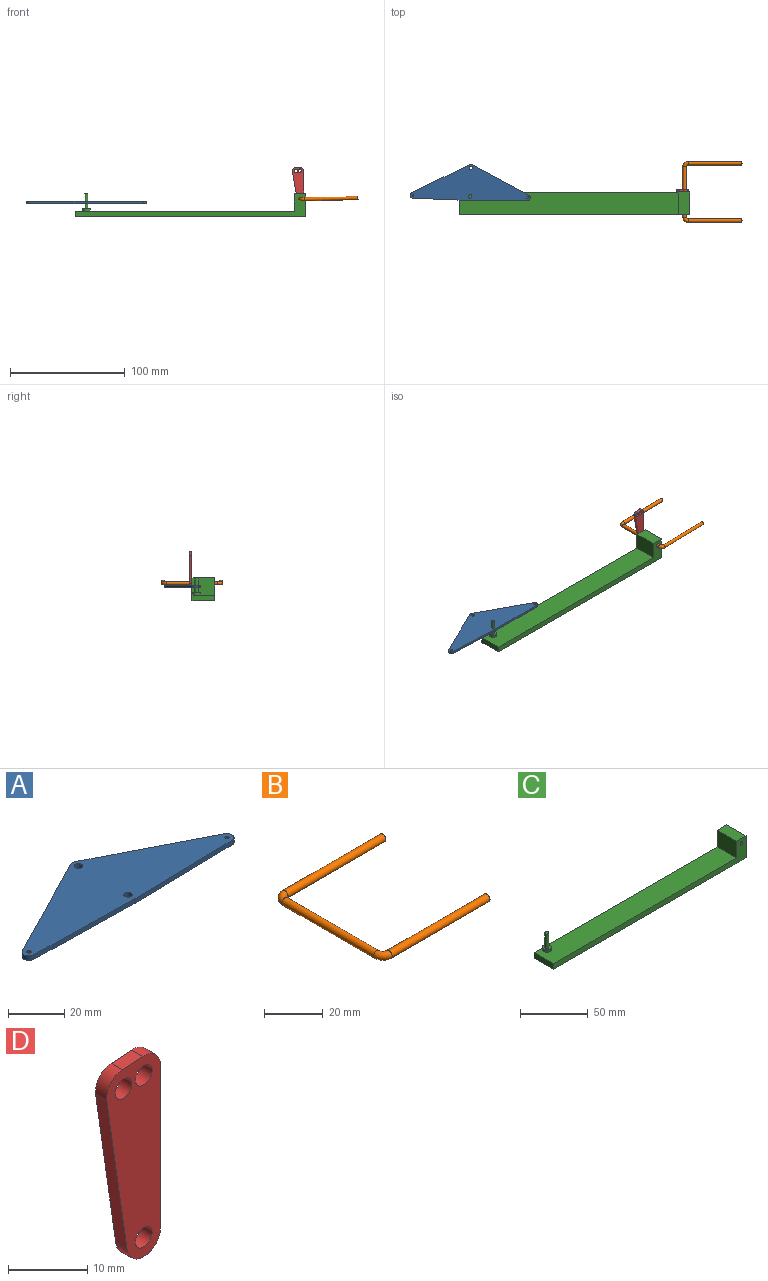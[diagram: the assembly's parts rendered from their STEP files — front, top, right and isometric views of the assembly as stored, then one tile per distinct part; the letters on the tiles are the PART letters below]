
ASSEMBLY  parts=4 mates=3
PART A: 14 faces, bbox 105x31.5x2 mm
  f0: plane 49.77x25.45mm, normal (-0.46,0.89,0), area 111.8mm2, adj f1,f11,f12,f13
  f1: cylinder r=2.5mm len=4.73mm, axis (0,0,1), area 13.2mm2, adj f0,f2,f12,f13
  f2: plane 49.98x2mm, normal (-0.02,-1,0), area 100mm2, adj f1,f3,f12,f13
  f3: plane 2x0.14mm, normal (0,-1,0), area 0.3mm2, adj f2,f4,f12,f13
  f4: plane 49.98x2mm, normal (0.02,-1,0), area 100mm2, adj f3,f5,f12,f13
  f5: cylinder r=2.5mm len=4.73mm, axis (0,0,1), area 13.2mm2, adj f4,f6,f12,f13
  f6: plane 49.77x25.45mm, normal (0.46,0.89,0), area 111.8mm2, adj f5,f11,f12,f13
  f7: cylinder r=0.75mm len=2mm, axis (0,0,1), area 9.4mm2, adj f12,f13
  f8: cylinder r=0.75mm len=2mm, axis (0,0,1), area 9.4mm2, adj f12,f13
  f9: cylinder r=1.5mm len=3mm, axis (0,0,1), area 18.8mm2, adj f12,f13
  f10: cylinder r=1.5mm len=3mm, axis (0,0,1), area 18.8mm2, adj f12,f13
  f11: cylinder r=3mm len=2.73mm, axis (0,0,1), area 5.7mm2, adj f0,f6,f12,f13
  f12: plane 105x31.5mm, normal (0,0,1), area 1860.8mm2, adj f0,f1,f2,f3,f4,f5,f6,f7
  f13: plane 105x31.5mm, normal (0,0,-1), area 1860.8mm2, adj f0,f1,f2,f3,f4,f5,f6,f7
PART B: 7 faces, bbox 51.9x53.7x3 mm
  f0: plane 3x3mm, normal (1,0,0), area 7.1mm2, adj f2
  f1: plane 3x3mm, normal (1,0,0), area 7.1mm2, adj f6
  f2: cylinder r=1.5mm len=47mm, axis (-1,0,0), area 443mm2, adj f0,f3
  f3: torus R=3mm, axis (0,0,1), area 44.4mm2, adj f2,f4
  f4: cylinder r=1.5mm len=44mm, axis (0,-1,0), area 414.7mm2, adj f3,f5
  f5: torus R=3mm, axis (0,0,1), area 44.4mm2, adj f4,f6
  f6: cylinder r=1.5mm len=47mm, axis (1,0,0), area 443mm2, adj f1,f5
PART C: 13 faces, bbox 201.1x20x20 mm
  f0: plane 201.05x20mm, normal (0,-1,0), area 1148.2mm2, adj f2,f3,f4,f9,f10,f11,f12
  f1: plane 201.05x20mm, normal (0,1,0), area 1148.2mm2, adj f2,f3,f4,f9,f10,f11,f12
  f2: plane 20x5mm, normal (-1,0,0), area 100mm2, adj f0,f1,f3,f4
  f3: plane 191.05x20mm, normal (0,0,1), area 3785.5mm2, adj f0,f1,f2,f5,f9
  f4: plane 201.05x20mm, normal (0,0,-1), area 4021.1mm2, adj f0,f1,f2,f10
  f5: cylinder r=3.36mm len=6.73mm, axis (0,0,1), area 42.3mm2, adj f3,f6
  f6: plane 6.73x6.73mm, normal (0,0,1), area 28.5mm2, adj f5,f7
  f7: cylinder r=1.5mm len=13mm, axis (0,0,1), area 122.5mm2, adj f6,f8
  f8: plane 3x3mm, normal (0,0,1), area 7.1mm2, adj f7
  f9: plane 20x15mm, normal (-1,0,0), area 300mm2, adj f0,f1,f3,f11
  f10: plane 20x20mm, normal (1,0,0), area 400mm2, adj f0,f1,f4,f11
  f11: plane 20x10mm, normal (0,0,1), area 200mm2, adj f0,f1,f9,f10
  f12: cylinder r=1.5mm len=20mm, axis (0,1,0), area 188.5mm2, adj f0,f1
PART D: 11 faces, bbox 9.6x2x31 mm
  f0: cylinder r=3mm len=5.97mm, axis (0,-1,0), area 18mm2, adj f1,f8,f9,f10
  f1: plane 25x2mm, normal (1,0,0), area 50mm2, adj f0,f2,f9,f10
  f2: cylinder r=3mm len=3.22mm, axis (0,-1,0), area 9.9mm2, adj f1,f3,f9,f10
  f3: plane 3.6x2mm, normal (-0.07,0,1), area 7.2mm2, adj f2,f4,f9,f10
  f4: cylinder r=3mm len=3.42mm, axis (0,-1,0), area 9.9mm2, adj f3,f8,f9,f10
  f5: cylinder r=1.5mm len=3mm, axis (0,-1,0), area 18.8mm2, adj f9,f10
  f6: cylinder r=1.5mm len=3mm, axis (0,-1,0), area 18.8mm2, adj f9,f10
  f7: cylinder r=1.5mm len=3mm, axis (0,-1,0), area 18.8mm2, adj f9,f10
  f8: plane 24.74x3.6mm, normal (-0.99,0,-0.14), area 50mm2, adj f0,f4,f9,f10
  f9: plane 31x9.6mm, normal (0,-1,0), area 212.9mm2, adj f0,f1,f2,f3,f4,f5,f6,f7
  f10: plane 31x9.6mm, normal (0,1,0), area 212.9mm2, adj f0,f1,f2,f3,f4,f5,f6,f7
PLACE A rot(axis=(0,0,-1),1.2deg) t=(39.99,-7.96,8.66)mm
PLACE B rot(axis=(0,-1,0),1.3deg) t=(236.19,-31.37,13.65)mm
PLACE C t=(-10.21,11.97,-2.84)mm fixed
PLACE D rot(axis=(0,-1,0),1.3deg) t=(186.2,13.97,12.5)mm
MATE revolute C.f7 <-> A.f10  axis (0,0,1) through (-0.65,8.08,10.66)mm
MATE revolute B.f4 <-> C.f12  axis (0,-1,0) through (186.2,11.97,12.5)mm
MATE fastened D.f7 <-> B.f4  axis (0,-1,0) through (186.2,11.97,12.5)mm
